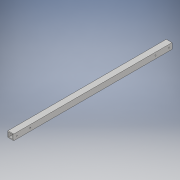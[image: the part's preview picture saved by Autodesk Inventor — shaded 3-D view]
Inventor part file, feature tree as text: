
AUTODESK INVENTOR PART (.ipt)
format: ipt  version: 2018 (Build 220112000, 112)  size: 118,784 bytes
history: native  units: in
note: dims shown in document units (in); Inventor stores cm internally (conversion verified against a paired STEP export)
features: extrude x2, sketch x2
ambient origin geometry x8: Origin, YZ Plane, XZ Plane, XY Plane, X Axis, Y Axis, Z Axis, Center Point
bodies: Solid1 (feature_tree)
feature tree (4):
  extrude  "Extrusion1"  Depth=1.0in
  extrude  "Extrusion3"  Depth=27.362in TaperAngle=0.0deg
  sketch  "Sketch1"  dims[d0=1.0in d1=1.0in]
  sketch  "Sketch2"  dims[d2=0.125in d3=27.362in d4=0.0in d5=0.5in d7=0.5in d8=0.197in d11=2.362in d12=2.362in d13=27.362in d14=0.0in]
